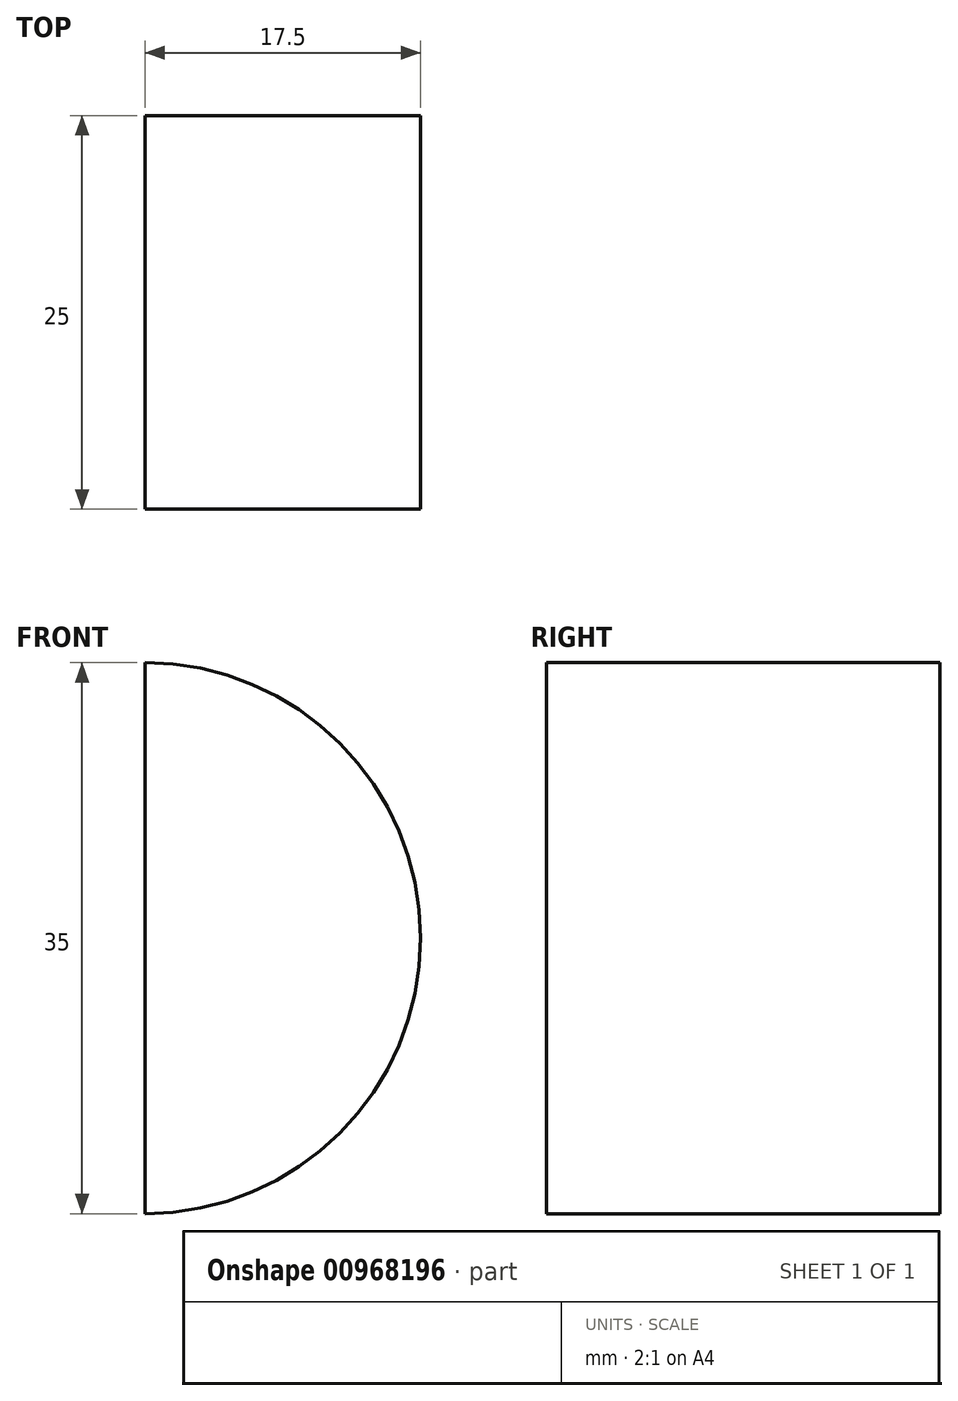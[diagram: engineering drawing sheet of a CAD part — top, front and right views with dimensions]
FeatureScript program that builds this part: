
annotation { "Feature Type Name" : "Feature", "Feature Type Description" : "" }
export const myFeature = defineFeature(function(context is Context, id is Id, definition is map)
    precondition{}
    {
        {
            var Q0;
            Q0=qCreatedBy(makeId("Front.planeOp"),FACE);
            var sketch = newSketch(context, id + "F0", { "sketchPlane" : qUnion([Q0])});
            skArc(sketch, "E0", {"start": v(0, -17.5) * mm, "mid": v(17.5, 0) * mm, "end": v(0, 17.5) * mm});
            skLineSegment(sketch, "E1", {"start": v(0, -17.5) * mm, "end": v(0, 17.5) * mm});
            skPoint(sketch, "E2.orphan", {"position": v(0, -29.84) * mm});
            skSolve(sketch);
        }
        {
            var Q0;
            Q0 = qSketchRegion(id + "F0", true);
            extrude(context, id + "F1", {"entities" : qUnion([Q0]), "depth" : 25 * mm, "offsetDistance" : 25 * mm});
        }
    });
